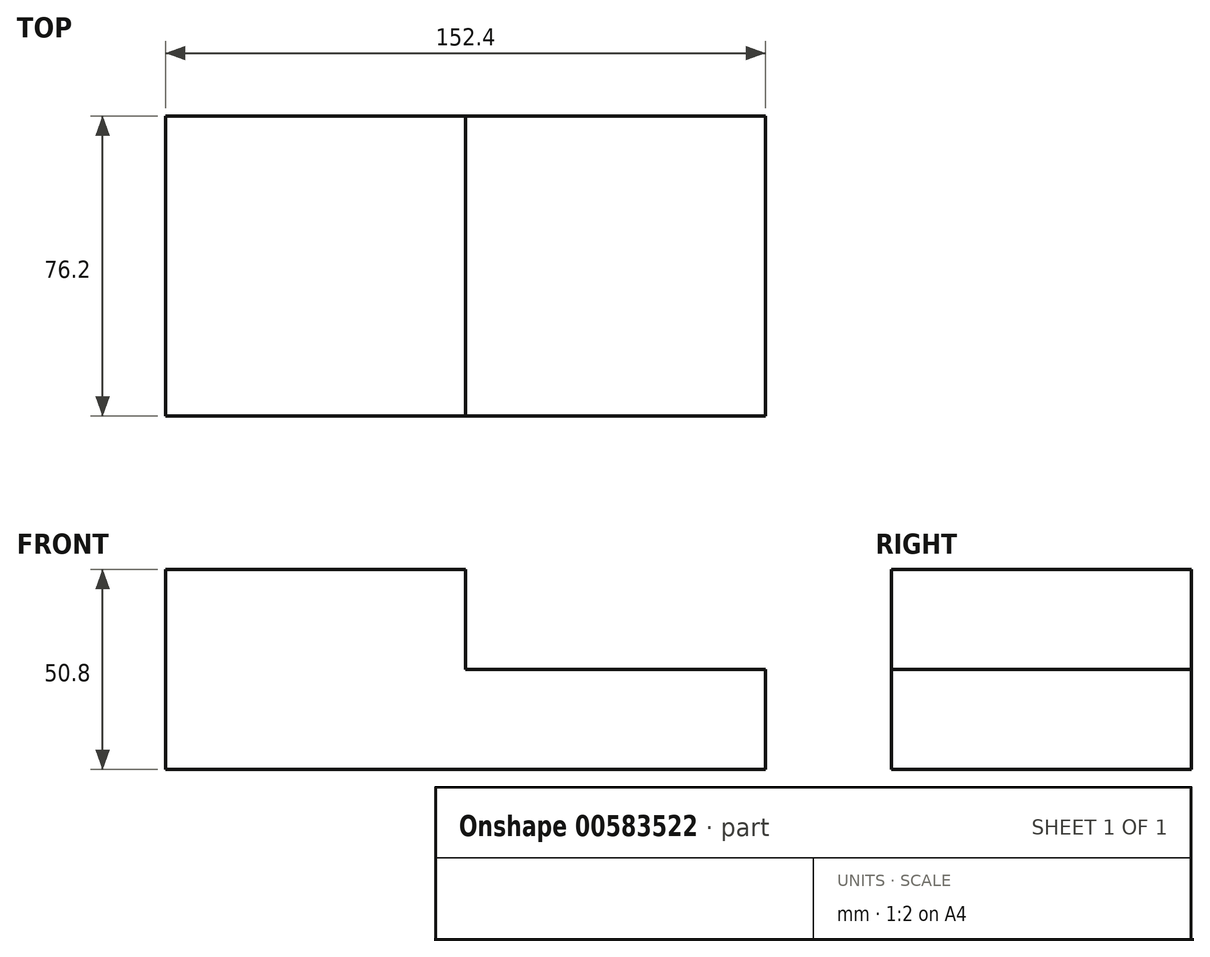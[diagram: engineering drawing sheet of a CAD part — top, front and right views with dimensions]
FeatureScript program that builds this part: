
annotation { "Feature Type Name" : "Feature", "Feature Type Description" : "" }
export const myFeature = defineFeature(function(context is Context, id is Id, definition is map)
    precondition{}
    {
        {
            var Q0;
            Q0=qCreatedBy(makeId("Front.planeOp"),FACE);
            var sketch = newSketch(context, id + "F0", { "sketchPlane" : qUnion([Q0])});
            skLineSegment(sketch, "E0", {"start": v(0, 0) * mm, "end": v(0, 50.8) * mm});
            skLineSegment(sketch, "E1", {"start": v(0, 50.8) * mm, "end": v(76.2, 50.8) * mm});
            skLineSegment(sketch, "E2", {"start": v(76.2, 50.8) * mm, "end": v(76.2, 25.4) * mm});
            skLineSegment(sketch, "E3", {"start": v(76.2, 25.4) * mm, "end": v(152.4, 25.4) * mm});
            skLineSegment(sketch, "E4", {"start": v(152.4, 25.4) * mm, "end": v(152.4, 0) * mm});
            skLineSegment(sketch, "E5", {"start": v(152.4, 0) * mm, "end": v(0, 0) * mm});
            skLineSegment(sketch, "E6", {"start": v(76.2, 25.4) * mm, "end": v(76.2, 50.8) * mm});
            skSolve(sketch);
        }
        {
            var Q0;
            Q0=makeQuery(id+"F0.imprint","IMPRINT",FACE,{"disambiguationData":[TD([[makeQuery(id+"F0.imprint","IMPRINT",EDGE,{"derivedFrom":sQuery(id+"F0.wireOp",EDGE,"E0")}),-1.0]])]});
            extrude(context, id + "F1", {"entities" : qUnion([Q0]), "depth" : 76.2 * mm, "offsetDistance" : 25.4 * mm});
        }
    });
